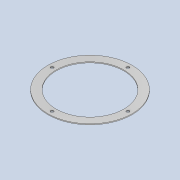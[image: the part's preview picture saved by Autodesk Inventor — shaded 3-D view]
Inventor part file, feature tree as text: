
AUTODESK INVENTOR PART (.ipt)
format: ipt  version: 2020.3 (Build 243373010, 373A)  size: 93,696 bytes
history: native  units: mm
features: sketch x2, extrude x1, hole x1
ambient origin geometry x8: Origin, YZ Plane, XZ Plane, XY Plane, X Axis, Y Axis, Z Axis, Center Point
bodies: Solid1 (feature_tree)
feature tree (4):
  extrude  "Extrusion1"  Depth=9.0mm
  hole  "Hole1"  [1 undecoded]
  sketch  "Sketch2"  dims[d14=75.0mm d15=9.0mm]
  sketch  "Sketch3"  dims[d16=1.0mm d17=0.0mm d18=3.242mm d19=8.0mm d20=4.0mm d21=2.0mm d22=90.0deg d23=11.8mm d24=0.0mm]
note: 1 required parameter value undecoded (feature->parameter linkage not recoverable at this tier; creation-order binding heuristic only, values carry confidence <= 0.55)
